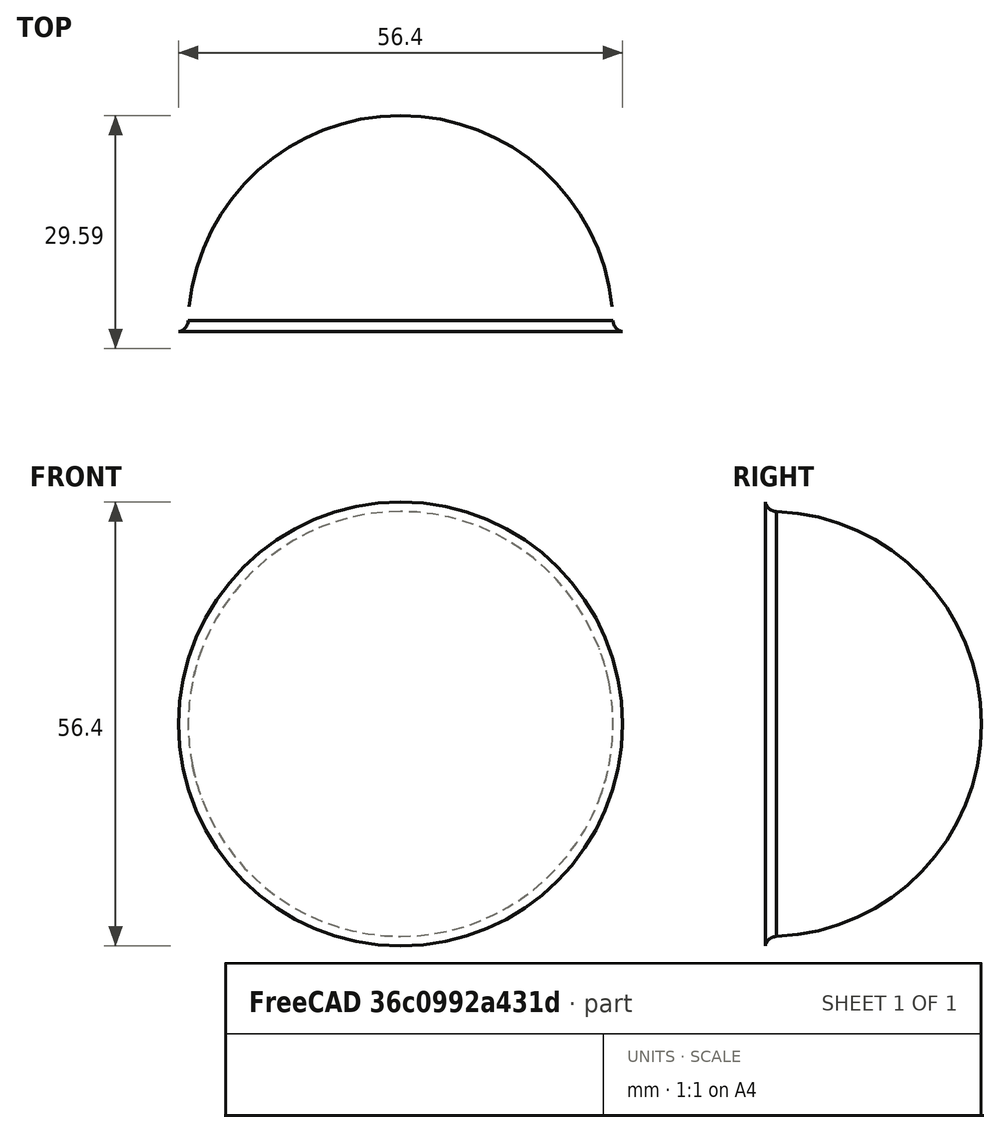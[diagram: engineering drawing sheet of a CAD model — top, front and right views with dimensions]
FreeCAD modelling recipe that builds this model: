
FCSTD DOCUMENT  (FreeCAD 1.0R39109 (Git))
Label: Cree LED Lens
License: All rights reserved
LicenseURL: http://en.wikipedia.org/wiki/All_rights_reserved
objects: Part::Feature×1, Part::Scale×1, Measure::MeasureRadius×1, Measure::MeasurePython×1, App::DocumentObjectGroup×1
note: 2 computed .brp shape members not serialized (recipe doc carries the construction recipe); baked Part::Feature solids carry a one-line shape summary decoded from their .brp

FEATURE [Part::Feature] Part__Feature  label="Cree XLamp XM-L LED LENS"
  shape: bbox 5.141 x 3.616 x 5.141 mm, 3 faces (baked)
FEATURE [Part::Scale] Scale  label="LED Lens Scale"
  Base = -> Part__Feature
  Uniform = true
  UniformScale = 12
  XScale = 1
  YScale = 1
  ZScale = 1
FEATURE [Measure::MeasureRadius] Radius  label="Radius: 28.20 mm"
  Element = -> Scale [Edge3]
  Radius = 28.2
FEATURE [Measure::MeasurePython] Center_of_Mass  label="Center_of_Mass: "  # WARN: FeaturePython — macro-defined, semantics opaque (R4)
  Result = (0,0,0)
FEATURE [App::DocumentObjectGroup] Measurements
  Group = -> [Radius,Center_of_Mass]
